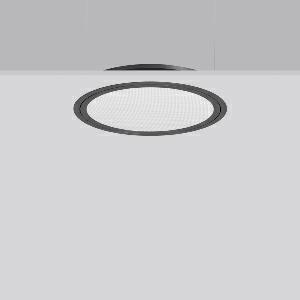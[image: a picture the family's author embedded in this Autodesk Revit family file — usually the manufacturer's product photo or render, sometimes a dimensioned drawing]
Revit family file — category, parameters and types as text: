
# Revit family: triona_round_e_312423_0031_2_12_b75a
name_source: partatom
category: Lighting Fixtures
units: mm (PartAtom-declared; Revit-internal decimal feet)

## family parameters
Cut with Voids When Loaded = No
Host = Face
Light Source = No
Part Type = Normal
Room Calculation Point = No
Round Connector Dimension = Use Diameter
Shared = No

## types (1)
- TuneableWhite 846 (1 x LED Modul 846, 2700 lm, 4600)
    Apparent Load = 29 VA
    CIE Flux Codes = 58 87 97 100 100
    Color Rendering = 80
    Color Temperature = 4600
    Default Elevation = 1800 mm
    Description = Series: TRIONA round
Decorative round LED recessed surface luminaire. Cover made of sheet steel, powder-coated. Frame made of aluminium, powder-coated. Recessed ring: aluminium extrusion profile, powder coated. Light emission through a diffuser in plastic, opal/prismatic. Lightguide and diffuser made of non-yellowing plastic (PMMA). Lateral light emission (RZB SIDELITE technology) for above-average homogeneous light distribution. Tunable white versions, dynamically adjustable from 2700 K to 6500 K. Suitable for installation in cavity ceilings. Tool-free mounting system thanks to the rocker arm mechanism (patent pending). Electronic ballast included. Very easy installation thanks to Plug+Play connection. Ideal for use as part of the Human Centric Lighting concept in connection with RZB light management systems. 
Colour: anthracite metallic (DB703)
Diameter: 505 mm
Height: 2 mm
Cut-out diameter: 482 mm
Recess height: 100 mm
Luminaire: recess height: 89 mm
Lamp: LED
Socket: without socket
Colour temperature: 2700K - 6500K
Colour rendering index (CRI): 80
System power: 29 W
Rated luminous flux: 2700 lm
Luminous efficiency: 93 lm/W
System power 2: 29 W
Rated luminous flux 2: 2550 lm
Luminous efficiency 2: 88 lm/W
System power 3: 30 W
Rated luminous flux 3: 2600 lm
Luminous efficiency 3: 87 lm/W
Control gear: Converter, dimmable, DALI
Protection class: I
Type of protection: IP 40
    Height = 0 mm  [stored 0 ft]
    Lamp = 1 x LED Modul 846
    Lamp Light Flux = 2700 lm
    Lamp count = 1
    Length = 505 mm
    Lifetime = 50000 h
    Luminous efficacy = 93 lm/W
    Manufacturer = RZB
    ModVariant = No
    Model = 312423.0031.2.12
    Mounting Place = Ceiling
    Mounting Type = Recessed
    Number of Poles = 1
    OnlyDefault = Yes
    Power Factor = 1
    Product Name = TRIONA round E
    Product group = Recessed modular luminaires
    ProductGroupID = 406
    Protection Class = Protection class I
    Protection Degree = IP 20
    RLX_Detail_Level = 1
    RLX_Emergency_Light_Flux = 0 lm
    RLX_Emergency_Type = 0
    RLX_Emergency_Type_DB = No
    RlxData = <blob elided: 35469 chars, md5=5eb8cd22>
    Socket = socket
    Standby Power = 0 W
    System Light Flux = 2700 lm
    System Power = 29 W
    Type Comments = TuneableWhite 846
    Type Image = 312423.0031.12.jpg
    URL = http://relux.com
    VarID = tuneablewhite_846
    Voltage = 230 V
    Voltage Range = 220-240 V
    Weight = 0.00 kg
    Width = 0 mm  [stored 0 ft]

note: [stored X ft] marks values corroborated as IEEE doubles in the binary element streams (Revit-internal decimal feet)

## geometry (parser evidence)
native form markers: Blend x4, Sweep x10
no freeform markers — native parametric forms only
